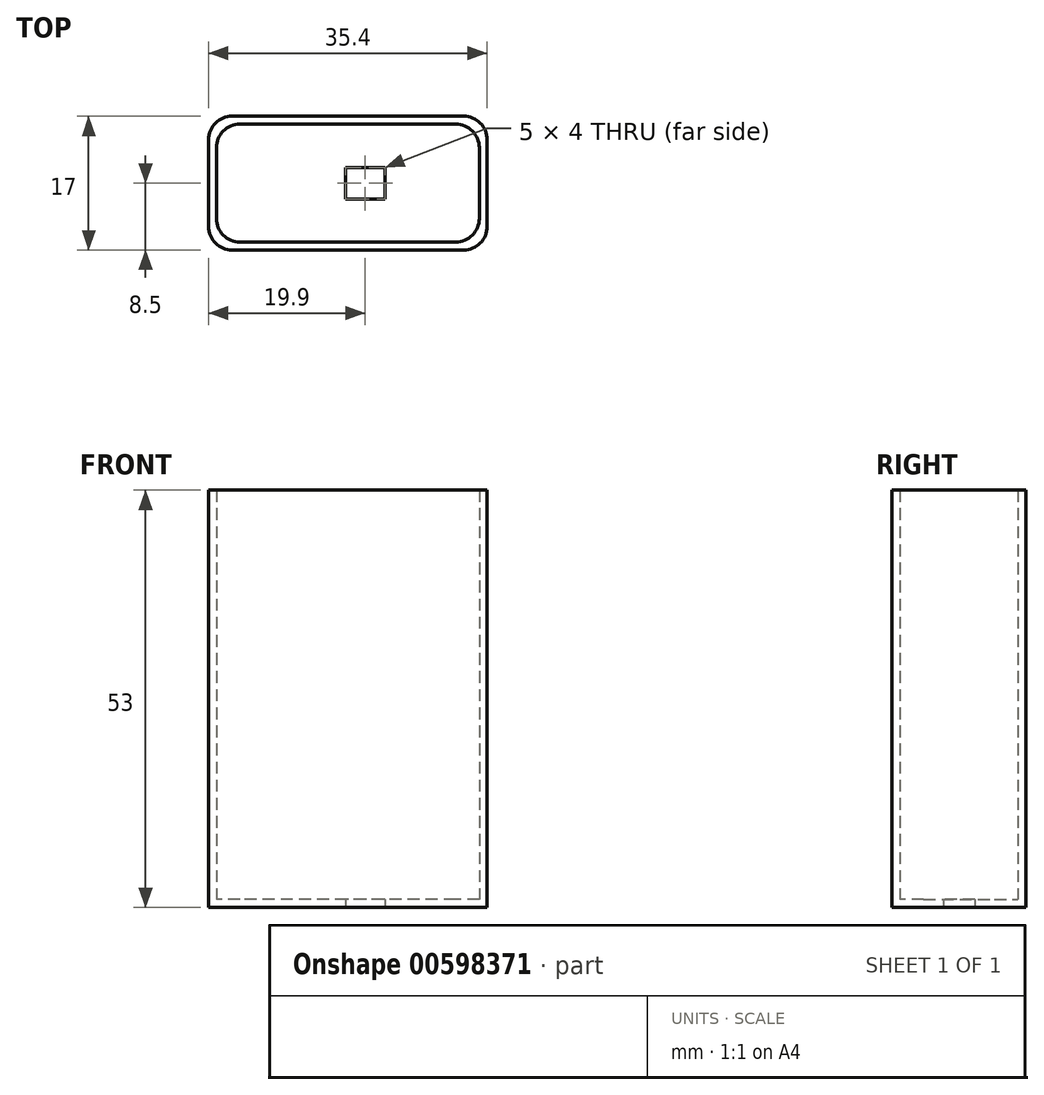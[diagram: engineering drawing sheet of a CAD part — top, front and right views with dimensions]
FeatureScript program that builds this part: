
annotation { "Feature Type Name" : "Feature", "Feature Type Description" : "" }
export const myFeature = defineFeature(function(context is Context, id is Id, definition is map)
    precondition{}
    {
        {
            var Q0;
            Q0=qCreatedBy(makeId("Top.planeOp"),FACE);
            var sketch = newSketch(context, id + "F0", { "sketchPlane" : qUnion([Q0])});
            skLineSegment(sketch, "E0.bottom", {"start": v(14.7, -8.5) * mm, "end": v(-14.7, -8.5) * mm});
            skLineSegment(sketch, "E0.top", {"start": v(14.7, 8.5) * mm, "end": v(-14.7, 8.5) * mm});
            skLineSegment(sketch, "E0.left", {"start": v(17.7, -5.5) * mm, "end": v(17.7, 5.5) * mm});
            skLineSegment(sketch, "E0.right", {"start": v(-17.7, -5.5) * mm, "end": v(-17.7, 5.5) * mm});
            skPoint(sketch, "E0.middle", {"position": v(0, 0) * mm});
            skLineSegment(sketch, "E1.0", {"start": v(13.7, 7.5) * mm, "end": v(-13.7, 7.5) * mm});
            skLineSegment(sketch, "E2.0", {"start": v(16.7, -4.5) * mm, "end": v(16.7, 4.5) * mm});
            skLineSegment(sketch, "E3.0", {"start": v(13.7, -7.5) * mm, "end": v(-13.7, -7.5) * mm});
            skLineSegment(sketch, "E4.0", {"start": v(-16.7, -4.5) * mm, "end": v(-16.7, 4.5) * mm});
            skPoint(sketch, "E5.visualSharp", {"position": v(-16.7, 7.5) * mm});
            skArc(sketch, "E5.filletArc", {"start": v(-13.7, 7.5) * mm, "mid": v(-15.82, 6.62) * mm, "end": v(-16.7, 4.5) * mm});
            skPoint(sketch, "E6.visualSharp", {"position": v(-17.7, 8.5) * mm});
            skArc(sketch, "E6.filletArc", {"start": v(-14.7, 8.5) * mm, "mid": v(-16.82, 7.62) * mm, "end": v(-17.7, 5.5) * mm});
            skPoint(sketch, "E7.visualSharp", {"position": v(16.7, 7.5) * mm});
            skArc(sketch, "E7.filletArc", {"start": v(16.7, 4.5) * mm, "mid": v(15.82, 6.62) * mm, "end": v(13.7, 7.5) * mm});
            skPoint(sketch, "E8.visualSharp", {"position": v(17.7, 8.5) * mm});
            skArc(sketch, "E8.filletArc", {"start": v(17.7, 5.5) * mm, "mid": v(16.82, 7.62) * mm, "end": v(14.7, 8.5) * mm});
            skPoint(sketch, "E9.visualSharp", {"position": v(16.7, -7.5) * mm});
            skArc(sketch, "E9.filletArc", {"start": v(13.7, -7.5) * mm, "mid": v(15.82, -6.62) * mm, "end": v(16.7, -4.5) * mm});
            skPoint(sketch, "E10.visualSharp", {"position": v(17.7, -8.5) * mm});
            skArc(sketch, "E10.filletArc", {"start": v(14.7, -8.5) * mm, "mid": v(16.82, -7.62) * mm, "end": v(17.7, -5.5) * mm});
            skPoint(sketch, "E11.visualSharp", {"position": v(-17.7, -8.5) * mm});
            skArc(sketch, "E11.filletArc", {"start": v(-17.7, -5.5) * mm, "mid": v(-16.82, -7.62) * mm, "end": v(-14.7, -8.5) * mm});
            skPoint(sketch, "E12.visualSharp", {"position": v(-16.7, -7.5) * mm});
            skArc(sketch, "E12.filletArc", {"start": v(-16.7, -4.5) * mm, "mid": v(-15.82, -6.62) * mm, "end": v(-13.7, -7.5) * mm});
            skSolve(sketch);
        }
        {
            var Q0;
            Q0=makeQuery(id+"F0.imprint","IMPRINT",FACE,{"disambiguationData":[TD([[makeQuery(id+"F0.imprint","IMPRINT",EDGE,{"derivedFrom":sQuery(id+"F0.wireOp",EDGE,"E0.bottom")}),-1.0]])]});
            extrude(context, id + "F1", {"entities" : qUnion([Q0]), "depth" : 53 * mm, "offsetDistance" : 25 * mm});
        }
        {
            var Q0;
            Q0=makeQuery(id+"F0.imprint","IMPRINT",FACE,{"disambiguationData":[TD([[makeQuery(id+"F0.imprint","IMPRINT",EDGE,{"derivedFrom":sQuery(id+"F0.wireOp",EDGE,"E1.0")}),1.0]])]});
            extrude(context, id + "F2", {"entities" : qUnion([Q0]), "operationType" : NewBodyOperationType.ADD, "depth" : 1 * mm, "offsetDistance" : 25 * mm});
        }
        {
            var Q0;
            {var subQ0=sQuery(id+"F0.wireOp",EDGE,"E12.filletArc");var subQ1=sQuery(id+"F0.wireOp",EDGE,"E9.filletArc");var subQ2=sQuery(id+"F0.wireOp",EDGE,"E7.filletArc");var subQ3=sQuery(id+"F0.wireOp",EDGE,"E5.filletArc");var subQ4=sQuery(id+"F0.wireOp",EDGE,"E4.0");var subQ5=sQuery(id+"F0.wireOp",EDGE,"E3.0");var subQ6=sQuery(id+"F0.wireOp",EDGE,"E2.0");var subQ7=sQuery(id+"F0.wireOp",EDGE,"E1.0");Q0=makeQuery(id+"F2.boolean.opBoolean","MERGE",FACE,{"derivedFrom":[makeQuery(id+"F1.opExtrude","CAP_FACE",FACE,{"disambiguationData":[OSD([sQuery(id+"F0.wireOp",EDGE,"E0.bottom"),sQuery(id+"F0.wireOp",EDGE,"E0.top"),sQuery(id+"F0.wireOp",EDGE,"E0.left"),sQuery(id+"F0.wireOp",EDGE,"E0.right"),subQ7,subQ6,subQ5,subQ4,subQ3,sQuery(id+"F0.wireOp",EDGE,"E6.filletArc"),subQ2,sQuery(id+"F0.wireOp",EDGE,"E8.filletArc"),subQ1,sQuery(id+"F0.wireOp",EDGE,"E10.filletArc"),sQuery(id+"F0.wireOp",EDGE,"E11.filletArc"),subQ0])],"isStart":true}),makeQuery(id+"F2.opExtrude","CAP_FACE",FACE,{"disambiguationData":[OSD([subQ7,subQ6,subQ5,subQ4,subQ3,subQ2,subQ1,subQ0])],"isStart":true})]});}
            var sketch = newSketch(context, id + "F3", { "sketchPlane" : qUnion([Q0])});
            skLineSegment(sketch, "E13.bottom", {"start": v(-0.3, 2) * mm, "end": v(4.7, 2) * mm});
            skLineSegment(sketch, "E13.top", {"start": v(-0.3, -2) * mm, "end": v(4.7, -2) * mm});
            skLineSegment(sketch, "E13.left", {"start": v(-0.3, 2) * mm, "end": v(-0.3, -2) * mm});
            skLineSegment(sketch, "E13.right", {"start": v(4.7, 2) * mm, "end": v(4.7, -2) * mm});
            skSolve(sketch);
        }
        {
            var Q0;
            Q0=makeQuery(id+"F3.imprint","IMPRINT",FACE,{"disambiguationData":[TD([[makeQuery(id+"F3.imprint","IMPRINT",EDGE,{"derivedFrom":sQuery(id+"F3.wireOp",EDGE,"E13.bottom")}),-1.0]])]});
            extrude(context, id + "F4", {"entities" : qUnion([Q0]), "operationType" : NewBodyOperationType.REMOVE, "endBound" : BoundingType.THROUGH_ALL, "oppositeDirection" : true, "depth" : 25 * mm, "offsetDistance" : 25 * mm});
        }
    });
